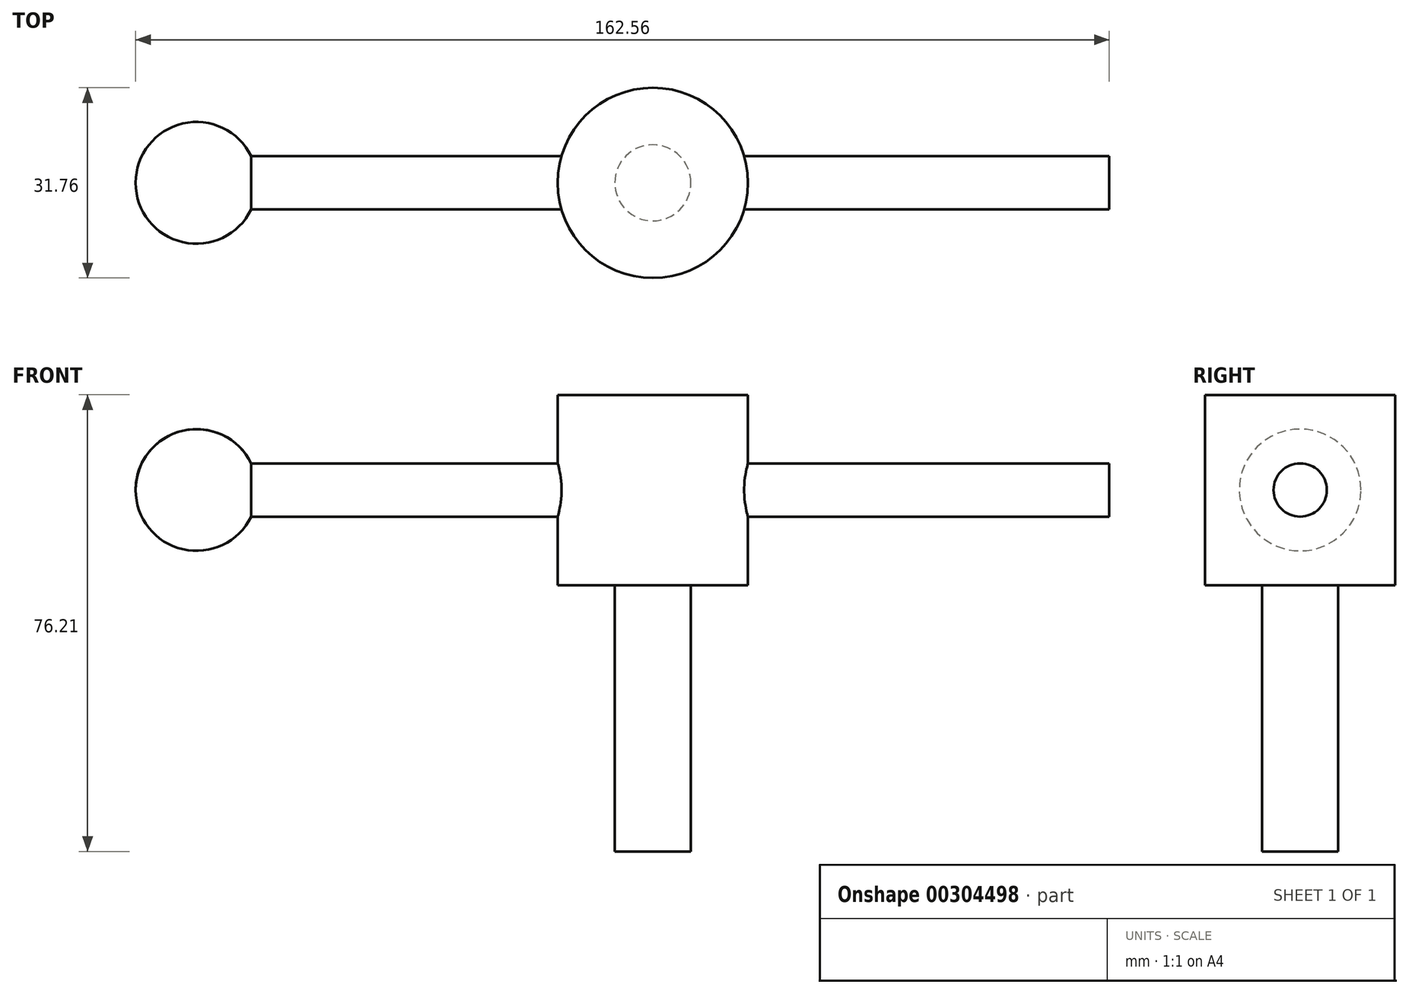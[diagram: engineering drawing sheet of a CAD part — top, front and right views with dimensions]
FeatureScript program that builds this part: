
annotation { "Feature Type Name" : "Feature", "Feature Type Description" : "" }
export const myFeature = defineFeature(function(context is Context, id is Id, definition is map)
    precondition{}
    {
        {
            var Q0;
            Q0=qCreatedBy(makeId("Front.planeOp"),FACE);
            var sketch = newSketch(context, id + "F0", { "sketchPlane" : qUnion([Q0])});
            skCircle(sketch, "E0", {"center": v(-76.2, 0) * mm, "radius": 10.16 * mm});
            skCircle(sketch, "E1.MirrorC", {"center": v(76.2, 0) * mm, "radius": 10.16 * mm});
            skLineSegment(sketch, "E2", {"start": v(-86.36, 0) * mm, "end": v(86.36, 0) * mm});
            skSolve(sketch);
        }
        {
            var Q0;
            {var subQ0=sQuery(id+"F0.wireOp",EDGE,"E2");var subQ1=sQuery(id+"F0.wireOp",EDGE,"E0");var subQ2=makeQuery(id+"F0.imprint","INTERSECT",VERTEX,{"disambiguationData":[OD(0.0)],"derivedFrom":[subQ1,subQ0]});Q0=makeQuery(id+"F0.imprint","IMPRINT",FACE,{"disambiguationData":[TD([[makeQuery(id+"F0.imprint","IMPRINT",EDGE,{"disambiguationData":[TD([[subQ2,1.0]])],"derivedFrom":subQ1}),1.0]])]});}
            var Q1;
            {var subQ0=sQuery(id+"F0.wireOp",EDGE,"E2");var subQ1=sQuery(id+"F0.wireOp",EDGE,"E1.MirrorC");var subQ2=makeQuery(id+"F0.imprint","INTERSECT",VERTEX,{"disambiguationData":[OD(0.0)],"derivedFrom":[subQ1,subQ0]});Q1=makeQuery(id+"F0.imprint","IMPRINT",FACE,{"disambiguationData":[TD([[makeQuery(id+"F0.imprint","IMPRINT",EDGE,{"disambiguationData":[TD([[subQ2,1.0]])],"derivedFrom":subQ1}),-1.0]])]});}
            var Q2;
            Q2=sQuery(id+"F0.wireOp",EDGE,"E2");
            revolve(context, id + "F1", {"entities" : qUnion([Q0, Q1]), "axis" : qUnion([Q2]), "revolveType" : RevolveType.FULL});
        }
        {
            var Q0;
            Q0=qCreatedBy(makeId("Right.planeOp"),FACE);
            var sketch = newSketch(context, id + "F2", { "sketchPlane" : qUnion([Q0])});
            skCircle(sketch, "E3", {"center": v(0, 0) * mm, "radius": 4.45 * mm});
            skSolve(sketch);
        }
        {
            var Q0;
            Q0 = qSketchRegion(id + "F2", true);
            extrude(context, id + "F3", {"entities" : qUnion([Q0]), "operationType" : NewBodyOperationType.ADD, "endBound" : BoundingType.SYMMETRIC, "depth" : 152.4 * mm, "hasSecondDirection" : true, "secondDirectionBound" : SecondDirectionBoundingType.UP_TO_SURFACE, "secondDirectionOppositeDirection" : true, "secondDirectionDepth" : 25.4 * mm});
        }
        {
            var Q0;
            Q0=qCreatedBy(makeId("Top.planeOp"),FACE);
            var sketch = newSketch(context, id + "F4", { "sketchPlane" : qUnion([Q0])});
            skCircle(sketch, "E4", {"center": v(0, 0) * mm, "radius": 15.88 * mm});
            skSolve(sketch);
        }
        {
            var Q0;
            Q0 = qSketchRegion(id + "F4", true);
            extrude(context, id + "F5", {"entities" : qUnion([Q0]), "operationType" : NewBodyOperationType.ADD, "endBound" : BoundingType.SYMMETRIC, "depth" : 31.75 * mm});
        }
        {
            var Q0;
            Q0=makeQuery(id+"F5.opExtrude","CAP_FACE",FACE,{"disambiguationData":[OSD([sQuery(id+"F4.wireOp",EDGE,"E4")])],"isStart":false});
            var sketch = newSketch(context, id + "F6", { "sketchPlane" : qUnion([Q0])});
            skCircle(sketch, "E5", {"center": v(0, 0) * mm, "radius": 6.35 * mm});
            skSolve(sketch);
        }
        {
            var Q0;
            Q0 = qSketchRegion(id + "F6", true);
            extrude(context, id + "F7", {"entities" : qUnion([Q0]), "operationType" : NewBodyOperationType.ADD, "oppositeDirection" : true, "depth" : 76.2 * mm});
        }
    });
